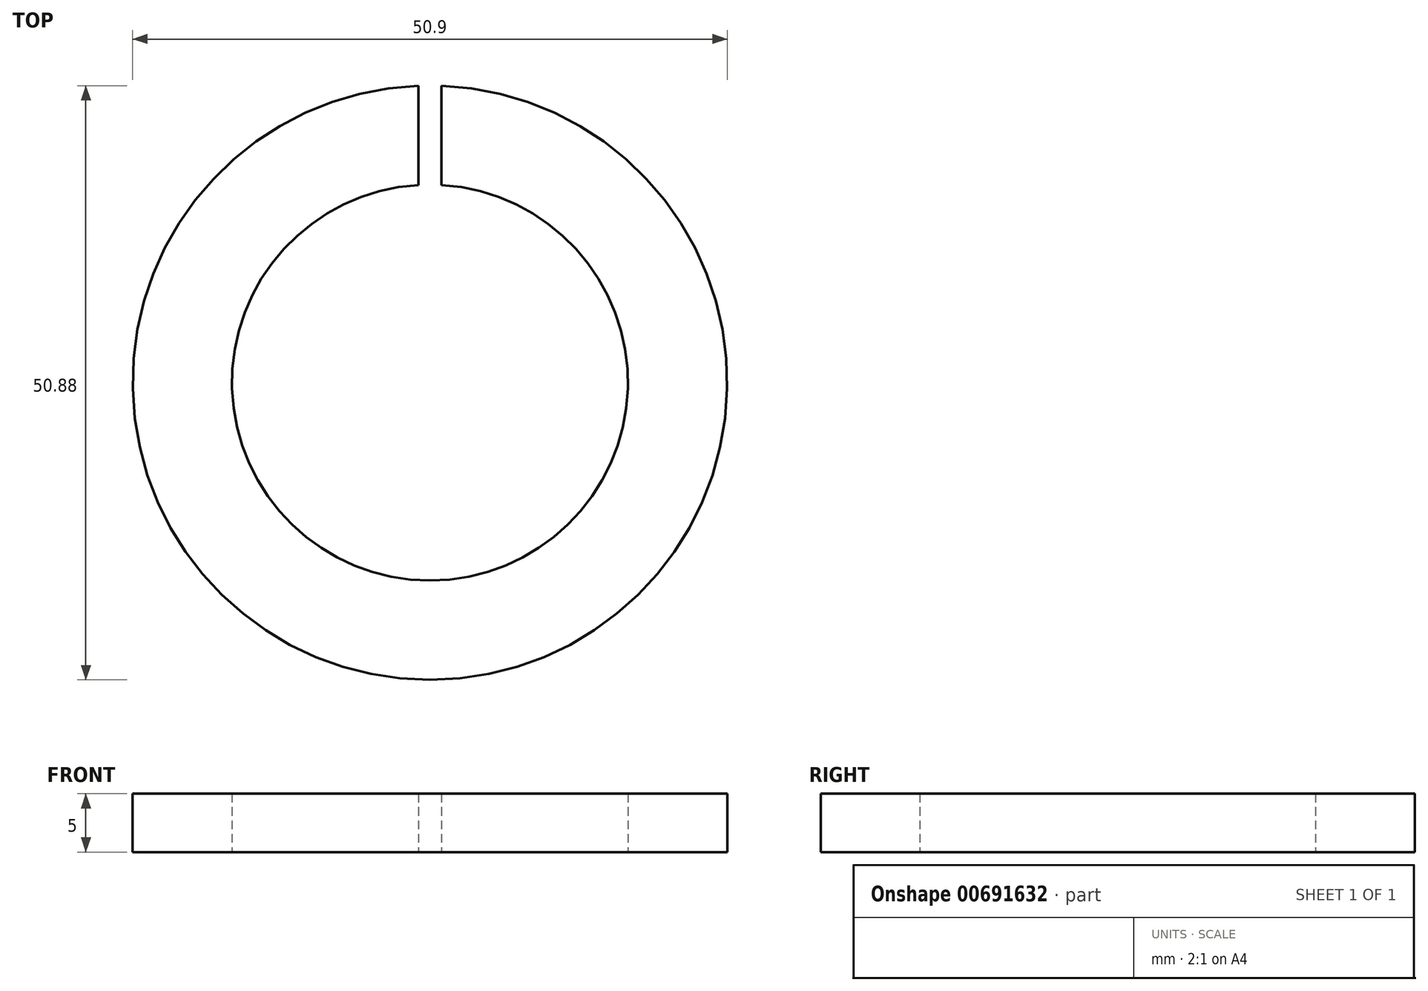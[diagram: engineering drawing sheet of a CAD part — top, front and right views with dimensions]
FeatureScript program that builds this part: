
annotation { "Feature Type Name" : "Feature", "Feature Type Description" : "" }
export const myFeature = defineFeature(function(context is Context, id is Id, definition is map)
    precondition{}
    {
        {
            var Q0;
            Q0=qCreatedBy(makeId("Top.planeOp"),FACE);
            var sketch = newSketch(context, id + "F0", { "sketchPlane" : qUnion([Q0])});
            skCircle(sketch, "E0", {"center": v(0, 0) * mm, "radius": 25.45 * mm});
            skCircle(sketch, "E1", {"center": v(0, 0) * mm, "radius": 16.95 * mm});
            skSolve(sketch);
        }
        {
            var Q0;
            Q0=makeQuery(id+"F0.imprint","IMPRINT",FACE,{"disambiguationData":[TD([[makeQuery(id+"F0.imprint","IMPRINT",EDGE,{"derivedFrom":sQuery(id+"F0.wireOp",EDGE,"E0")}),1.0]])]});
            extrude(context, id + "F1", {"entities" : qUnion([Q0]), "depth" : 5 * mm, "offsetDistance" : 25 * mm});
        }
        {
            var Q0;
            Q0=makeQuery(id+"F1.opExtrude","CAP_FACE",FACE,{"disambiguationData":[OSD([sQuery(id+"F0.wireOp",EDGE,"E0"),sQuery(id+"F0.wireOp",EDGE,"E1")])],"isStart":false});
            var sketch = newSketch(context, id + "F2", { "sketchPlane" : qUnion([Q0])});
            skLineSegment(sketch, "E2", {"start": v(0, 16.95) * mm, "end": v(0, 25.45) * mm, "construction": true});
            skLineSegment(sketch, "E3.bottom", {"start": v(1, 28.7) * mm, "end": v(-1, 28.7) * mm});
            skLineSegment(sketch, "E3.top", {"start": v(1, 13.7) * mm, "end": v(-1, 13.7) * mm});
            skLineSegment(sketch, "E3.left", {"start": v(1, 28.7) * mm, "end": v(1, 13.7) * mm});
            skLineSegment(sketch, "E3.right", {"start": v(-1, 28.7) * mm, "end": v(-1, 13.7) * mm});
            skPoint(sketch, "E3.middle", {"position": v(0, 21.2) * mm});
            skSolve(sketch);
        }
        {
            var Q0;
            Q0 = qSketchRegion(id + "F2", true);
            extrude(context, id + "F3", {"entities" : qUnion([Q0]), "operationType" : NewBodyOperationType.REMOVE, "oppositeDirection" : true, "depth" : 25 * mm, "offsetDistance" : 25 * mm});
        }
    });
